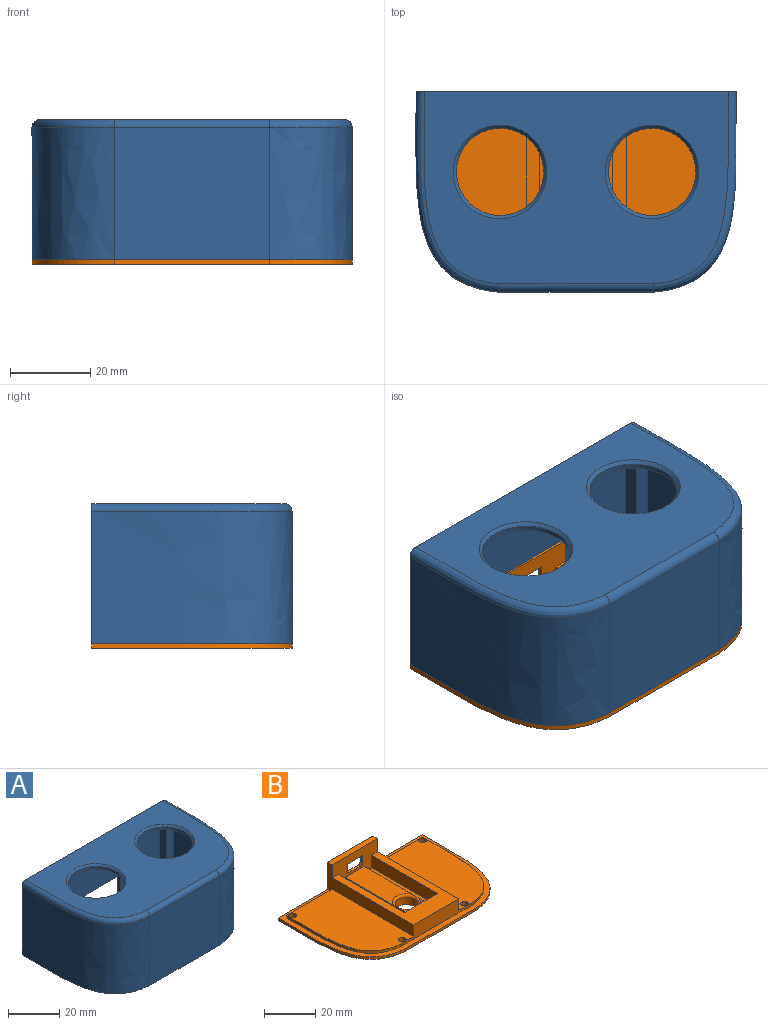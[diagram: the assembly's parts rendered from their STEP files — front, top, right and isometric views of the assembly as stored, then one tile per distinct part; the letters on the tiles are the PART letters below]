
ASSEMBLY  parts=2 mates=1
PART A: 303 faces, bbox 86.4x51x35.1 mm
  f0: plane 80.07x35.07mm, normal (0,1,0), area 2328.1mm2, adj f1,f9,f11,f12,f38,f39,f41,f42
  f1: plane 86.32x50mm, normal (0,0,-1), area 416.2mm2, adj f0,f2,f9,f10,f11,f18,f19,f20
  f2: plane 72.12x33mm, normal (0,-1,0), area 1919mm2, adj f1,f15,f16,f22,f23,f26,f27,f41
  f3: plane 31.4x4mm, normal (1,0,0), area 125.6mm2, adj f4,f15,f18,f29
  f4: plane 31.4x4mm, normal (0,1,0), area 125.6mm2, adj f3,f5,f15,f29
  f5: plane 31.4x4mm, normal (-1,0,0), area 125.6mm2, adj f4,f15,f19,f29
  f6: plane 31.4x4mm, normal (1,0,0), area 125.6mm2, adj f7,f15,f19,f28
  f7: plane 31.4x4mm, normal (0,1,0), area 125.6mm2, adj f6,f8,f15,f28
  f8: plane 31.4x4mm, normal (-1,0,0), area 125.6mm2, adj f7,f15,f20,f28
  f9: extruded ~50x33mm, area 2014.1mm2, adj f0,f1,f10,f38
  f10: plane 38.68x33mm, normal (0,-1,0), area 1276.3mm2, adj f1,f9,f11,f40
  f11: extruded ~50x33mm, area 2014.1mm2, adj f0,f1,f10,f39
  f12: plane 76.13x48.02mm, normal (0,0,1), area 2603mm2, adj f0,f38,f39,f40,f301,f302
  f13: cylinder r=10.9mm len=21.8mm, axis (0,0,1), area 82.2mm2, adj f15,f301
  f14: cylinder r=10.9mm len=21.8mm, axis (0,0,1), area 82.2mm2, adj f15,f302
  f15: plane 76.16x46mm, normal (0,0,-1), area 2501mm2, adj f2,f3,f4,f5,f6,f7,f8,f13
  f16: plane 31.4x4mm, normal (-1,0.03,0), area 125.6mm2, adj f2,f15,f17,f24
  f17: plane 31.4x4mm, normal (0,-1,0), area 125.6mm2, adj f15,f16,f18,f24
  f18: extruded ~42x33mm, area 1715.2mm2, adj f1,f3,f15,f17,f19,f25
  f19: plane 38.51x33mm, normal (0,1,0), area 1019.7mm2, adj f1,f5,f6,f15,f18,f20,f28,f29
  f20: extruded ~42x33mm, area 1715.1mm2, adj f1,f8,f15,f19,f21,f26
  f21: plane 31.4x4mm, normal (0,-1,0), area 125.6mm2, adj f15,f20,f22,f27
  f22: plane 31.4x4mm, normal (1,0,0), area 125.6mm2, adj f2,f15,f21,f27
  f23: plane 3.9x1.6mm, normal (0,-1,0), area 6.2mm2, adj f1,f2,f24,f25
  f24: plane 4x4mm, normal (0,0,-1), area 10.9mm2, adj f16,f17,f23,f25,f36
  f25: plane 4x1.6mm, normal (-1,0,0), area 6.4mm2, adj f1,f18,f23,f24
  f26: plane 4x1.6mm, normal (1,0,0), area 6.4mm2, adj f1,f2,f20,f27
  f27: plane 4x4mm, normal (0,0,-1), area 11.1mm2, adj f2,f21,f22,f26,f34
  f28: plane 4x4mm, normal (0,0,-1), area 11.1mm2, adj f6,f7,f8,f19,f32
  f29: plane 4x4mm, normal (0,0,-1), area 11.1mm2, adj f3,f4,f5,f19,f30
  f30: cylinder r=1.25mm len=23.4mm, axis (0,0,-1), area 183.8mm2, adj f29,f31
  f31: plane 2.5x2.5mm, normal (0,0,-1), area 4.9mm2, adj f30
  f32: cylinder r=1.25mm len=23.4mm, axis (0,0,-1), area 183.8mm2, adj f28,f33
  f33: plane 2.5x2.5mm, normal (0,0,-1), area 4.9mm2, adj f32
  f34: cylinder r=1.25mm len=23.4mm, axis (0,0,-1), area 183.8mm2, adj f27,f35
  f35: plane 2.5x2.5mm, normal (0,0,-1), area 4.9mm2, adj f34
  f36: cylinder r=1.25mm len=23.4mm, axis (0,0,-1), area 183.8mm2, adj f24,f37
  f37: plane 2.5x2.5mm, normal (0,0,-1), area 4.9mm2, adj f36
  f38: bspline ~50.91x21.41mm, area 188.2mm2, adj f0,f9,f12,f40
  f39: bspline ~50.91x21.41mm, area 188.2mm2, adj f0,f11,f12,f40
  f40: cylinder r=2mm len=38.68mm, axis (-1,0,0), area 121.2mm2, adj f10,f12,f38,f39
  f41: plane 13.2x2mm, normal (1,0,0), area 26.4mm2, adj f0,f1,f2,f43
  f42: plane 13.2x2mm, normal (-1,0,0), area 26.4mm2, adj f0,f1,f2,f43
  f43: plane 25.4x2mm, normal (0,0,-1), area 50.8mm2, adj f0,f2,f41,f42
  f44: plane 0.6x0.52mm, normal (-1,0,0), area 0.3mm2, adj f0,f45,f47,f48
  f45: plane 1.69x0.6mm, normal (0,0,1), area 1mm2, adj f0,f44,f46,f48
  f46: plane 0.6x0.52mm, normal (1,0,0), area 0.3mm2, adj f0,f45,f47,f48
  f47: plane 1.69x0.6mm, normal (0,0,-1), area 1mm2, adj f0,f44,f46,f48
  f48: plane 1.69x0.52mm, normal (0,1,0), area 0.9mm2, adj f44,f45,f46,f47
  f49: extruded ~0.84x0.6mm, area 0.6mm2, adj f50,f71,f72,f293
  f50: extruded ~0.8x0.6mm, area 0.5mm2, adj f49,f51,f72,f293
  f51: extruded ~1.1x0.6mm, area 0.7mm2, adj f50,f52,f72,f293
  f52: extruded ~1.1x0.6mm, area 0.7mm2, adj f51,f53,f72,f293
  f53: extruded ~0.79x0.6mm, area 0.5mm2, adj f52,f54,f72,f293
  f54: extruded ~0.85x0.6mm, area 0.6mm2, adj f53,f55,f72,f293
  f55: extruded ~1.14x0.6mm, area 0.7mm2, adj f54,f71,f72,f293
  f56: extruded ~1.16x0.6mm, area 0.8mm2, adj f0,f57,f70,f72
  f57: extruded ~1.19x0.6mm, area 0.8mm2, adj f0,f56,f58,f72
  f58: plane 0.6x0.03mm, normal (0,0,-1), area 0mm2, adj f0,f57,f59,f72
  f59: extruded ~0.79x0.6mm, area 0.5mm2, adj f0,f58,f60,f72
  f60: plane 1.3x0.6mm, normal (1,0,0), area 0.8mm2, adj f0,f59,f61,f72
  f61: plane 0.6x0.57mm, normal (0,0,-1), area 0.3mm2, adj f0,f60,f62,f72
  f62: plane 5.36x0.6mm, normal (-1,0,0), area 3.2mm2, adj f0,f61,f63,f72
  f63: plane 0.6x0.41mm, normal (0,0,1), area 0.2mm2, adj f0,f62,f64,f72
  f64: plane 0.6x0.49mm, normal (0.97,0,0.24), area 0.3mm2, adj f0,f63,f65,f72
  f65: plane 0.6x0.04mm, normal (0,0,1), area 0mm2, adj f0,f64,f66,f72
  f66: extruded ~0.6x0.51mm, area 0.4mm2, adj f0,f65,f67,f72
  f67: extruded ~0.67x0.6mm, area 0.4mm2, adj f0,f66,f68,f72
  f68: extruded ~1.15x0.6mm, area 0.8mm2, adj f0,f67,f69,f72
  f69: extruded ~1.45x0.6mm, area 0.9mm2, adj f0,f68,f70,f72
  f70: extruded ~1.44x0.6mm, area 0.9mm2, adj f0,f56,f69,f72
  f71: extruded ~1.13x0.6mm, area 0.7mm2, adj f49,f55,f72,f293
  f72: plane 5.43x3.33mm, normal (0,1,0), area 6.9mm2, adj f49,f50,f51,f52,f53,f54,f55,f56
  f73: extruded ~1.6x0.6mm, area 1mm2, adj f74,f88,f89,f294
  f74: extruded ~1.6x0.6mm, area 1mm2, adj f73,f75,f89,f294
  f75: extruded ~0.82x0.6mm, area 0.6mm2, adj f74,f76,f89,f294
  f76: extruded ~0.83x0.6mm, area 0.6mm2, adj f75,f77,f89,f294
  f77: extruded ~1.59x0.6mm, area 1mm2, adj f76,f78,f89,f294
  f78: extruded ~1.59x0.6mm, area 1mm2, adj f77,f79,f89,f294
  f79: extruded ~0.83x0.6mm, area 0.6mm2, adj f78,f88,f89,f294
  f80: extruded ~1.95x0.6mm, area 1.2mm2, adj f0,f81,f87,f89
  f81: extruded ~1.93x0.6mm, area 1.2mm2, adj f0,f80,f82,f89
  f82: extruded ~1.25x0.67mm, area 0.9mm2, adj f0,f81,f83,f89
  f83: extruded ~1.25x0.64mm, area 0.9mm2, adj f0,f82,f84,f89
  f84: extruded ~1.95x0.6mm, area 1.2mm2, adj f0,f83,f85,f89
  f85: extruded ~1.94x0.6mm, area 1.2mm2, adj f0,f84,f86,f89
  f86: extruded ~1.24x0.66mm, area 0.9mm2, adj f0,f85,f87,f89
  f87: extruded ~1.26x0.64mm, area 0.9mm2, adj f0,f80,f86,f89
  f88: extruded ~0.82x0.6mm, area 0.6mm2, adj f73,f79,f89,f294
  f89: plane 5.19x3.33mm, normal (0,1,0), area 6.7mm2, adj f73,f74,f75,f76,f77,f78,f79,f80
  f90: extruded ~1.6x0.6mm, area 1mm2, adj f91,f105,f106,f295
  f91: extruded ~1.6x0.6mm, area 1mm2, adj f90,f92,f106,f295
  f92: extruded ~0.82x0.6mm, area 0.6mm2, adj f91,f93,f106,f295
  f93: extruded ~0.83x0.6mm, area 0.6mm2, adj f92,f94,f106,f295
  f94: extruded ~1.59x0.6mm, area 1mm2, adj f93,f95,f106,f295
  f95: extruded ~1.59x0.6mm, area 1mm2, adj f94,f96,f106,f295
  f96: extruded ~0.83x0.6mm, area 0.6mm2, adj f95,f105,f106,f295
  f97: extruded ~1.95x0.6mm, area 1.2mm2, adj f0,f98,f104,f106
  f98: extruded ~1.93x0.6mm, area 1.2mm2, adj f0,f97,f99,f106
  f99: extruded ~1.25x0.67mm, area 0.9mm2, adj f0,f98,f100,f106
  f100: extruded ~1.25x0.64mm, area 0.9mm2, adj f0,f99,f101,f106
  f101: extruded ~1.95x0.6mm, area 1.2mm2, adj f0,f100,f102,f106
  f102: extruded ~1.94x0.6mm, area 1.2mm2, adj f0,f101,f103,f106
  f103: extruded ~1.24x0.66mm, area 0.9mm2, adj f0,f102,f104,f106
  f104: extruded ~1.26x0.64mm, area 0.9mm2, adj f0,f97,f103,f106
  f105: extruded ~0.82x0.6mm, area 0.6mm2, adj f90,f96,f106,f295
  f106: plane 5.19x3.33mm, normal (0,1,0), area 6.7mm2, adj f90,f91,f92,f93,f94,f95,f96,f97
  f107: extruded ~1.6x0.6mm, area 1mm2, adj f108,f122,f123,f296
  f108: extruded ~1.6x0.6mm, area 1mm2, adj f107,f109,f123,f296
  f109: extruded ~0.82x0.6mm, area 0.6mm2, adj f108,f110,f123,f296
  f110: extruded ~0.83x0.6mm, area 0.6mm2, adj f109,f111,f123,f296
  f111: extruded ~1.59x0.6mm, area 1mm2, adj f110,f112,f123,f296
  f112: extruded ~1.59x0.6mm, area 1mm2, adj f111,f113,f123,f296
  f113: extruded ~0.83x0.6mm, area 0.6mm2, adj f112,f122,f123,f296
  f114: extruded ~1.95x0.6mm, area 1.2mm2, adj f0,f115,f121,f123
  f115: extruded ~1.93x0.6mm, area 1.2mm2, adj f0,f114,f116,f123
  f116: extruded ~1.25x0.67mm, area 0.9mm2, adj f0,f115,f117,f123
  f117: extruded ~1.25x0.64mm, area 0.9mm2, adj f0,f116,f118,f123
  f118: extruded ~1.95x0.6mm, area 1.2mm2, adj f0,f117,f119,f123
  f119: extruded ~1.94x0.6mm, area 1.2mm2, adj f0,f118,f120,f123
  f120: extruded ~1.24x0.66mm, area 0.9mm2, adj f0,f119,f121,f123
  f121: extruded ~1.26x0.64mm, area 0.9mm2, adj f0,f114,f120,f123
  f122: extruded ~0.82x0.6mm, area 0.6mm2, adj f107,f113,f123,f296
  f123: plane 5.19x3.33mm, normal (0,1,0), area 6.7mm2, adj f107,f108,f109,f110,f111,f112,f113,f114
  f124: extruded ~1.6x0.6mm, area 1mm2, adj f125,f139,f140,f297
  f125: extruded ~1.6x0.6mm, area 1mm2, adj f124,f126,f140,f297
  f126: extruded ~0.82x0.6mm, area 0.6mm2, adj f125,f127,f140,f297
  f127: extruded ~0.83x0.6mm, area 0.6mm2, adj f126,f128,f140,f297
  f128: extruded ~1.59x0.6mm, area 1mm2, adj f127,f129,f140,f297
  f129: extruded ~1.59x0.6mm, area 1mm2, adj f128,f130,f140,f297
  f130: extruded ~0.83x0.6mm, area 0.6mm2, adj f129,f139,f140,f297
  f131: extruded ~1.95x0.6mm, area 1.2mm2, adj f0,f132,f138,f140
  f132: extruded ~1.93x0.6mm, area 1.2mm2, adj f0,f131,f133,f140
  f133: extruded ~1.25x0.67mm, area 0.9mm2, adj f0,f132,f134,f140
  f134: extruded ~1.25x0.64mm, area 0.9mm2, adj f0,f133,f135,f140
  f135: extruded ~1.95x0.6mm, area 1.2mm2, adj f0,f134,f136,f140
  f136: extruded ~1.94x0.6mm, area 1.2mm2, adj f0,f135,f137,f140
  f137: extruded ~1.24x0.66mm, area 0.9mm2, adj f0,f136,f138,f140
  f138: extruded ~1.26x0.64mm, area 0.9mm2, adj f0,f131,f137,f140
  f139: extruded ~0.82x0.6mm, area 0.6mm2, adj f124,f130,f140,f297
  f140: plane 5.19x3.33mm, normal (0,1,0), area 6.7mm2, adj f124,f125,f126,f127,f128,f129,f130,f131
  f141: extruded ~1.6x0.6mm, area 1mm2, adj f142,f156,f157,f298
  f142: extruded ~1.6x0.6mm, area 1mm2, adj f141,f143,f157,f298
  f143: extruded ~0.82x0.6mm, area 0.6mm2, adj f142,f144,f157,f298
  f144: extruded ~0.83x0.6mm, area 0.6mm2, adj f143,f145,f157,f298
  f145: extruded ~1.59x0.6mm, area 1mm2, adj f144,f146,f157,f298
  f146: extruded ~1.59x0.6mm, area 1mm2, adj f145,f147,f157,f298
  f147: extruded ~0.83x0.6mm, area 0.6mm2, adj f146,f156,f157,f298
  f148: extruded ~1.95x0.6mm, area 1.2mm2, adj f0,f149,f155,f157
  f149: extruded ~1.93x0.6mm, area 1.2mm2, adj f0,f148,f150,f157
  f150: extruded ~1.25x0.67mm, area 0.9mm2, adj f0,f149,f151,f157
  f151: extruded ~1.25x0.64mm, area 0.9mm2, adj f0,f150,f152,f157
  f152: extruded ~1.95x0.6mm, area 1.2mm2, adj f0,f151,f153,f157
  f153: extruded ~1.94x0.6mm, area 1.2mm2, adj f0,f152,f154,f157
  f154: extruded ~1.24x0.66mm, area 0.9mm2, adj f0,f153,f155,f157
  f155: extruded ~1.26x0.64mm, area 0.9mm2, adj f0,f148,f154,f157
  f156: extruded ~0.82x0.6mm, area 0.6mm2, adj f141,f147,f157,f298
  f157: plane 5.19x3.33mm, normal (0,1,0), area 6.7mm2, adj f141,f142,f143,f144,f145,f146,f147,f148
  f158: extruded ~1.6x0.6mm, area 1mm2, adj f159,f173,f174,f299
  f159: extruded ~1.6x0.6mm, area 1mm2, adj f158,f160,f174,f299
  f160: extruded ~0.82x0.6mm, area 0.6mm2, adj f159,f161,f174,f299
  f161: extruded ~0.83x0.6mm, area 0.6mm2, adj f160,f162,f174,f299
  f162: extruded ~1.59x0.6mm, area 1mm2, adj f161,f163,f174,f299
  f163: extruded ~1.59x0.6mm, area 1mm2, adj f162,f164,f174,f299
  f164: extruded ~0.83x0.6mm, area 0.6mm2, adj f163,f173,f174,f299
  f165: extruded ~1.95x0.6mm, area 1.2mm2, adj f0,f166,f172,f174
  f166: extruded ~1.93x0.6mm, area 1.2mm2, adj f0,f165,f167,f174
  f167: extruded ~1.25x0.67mm, area 0.9mm2, adj f0,f166,f168,f174
  f168: extruded ~1.25x0.64mm, area 0.9mm2, adj f0,f167,f169,f174
  f169: extruded ~1.95x0.6mm, area 1.2mm2, adj f0,f168,f170,f174
  f170: extruded ~1.94x0.6mm, area 1.2mm2, adj f0,f169,f171,f174
  f171: extruded ~1.24x0.66mm, area 0.9mm2, adj f0,f170,f172,f174
  f172: extruded ~1.26x0.64mm, area 0.9mm2, adj f0,f165,f171,f174
  f173: extruded ~0.82x0.6mm, area 0.6mm2, adj f158,f164,f174,f299
  f174: plane 5.19x3.33mm, normal (0,1,0), area 6.7mm2, adj f158,f159,f160,f161,f162,f163,f164,f165
  f175: plane 0.6x0.56mm, normal (0,0,1), area 0.3mm2, adj f0,f176,f183,f184
  f176: plane 5.04x0.6mm, normal (1,0,0), area 3mm2, adj f0,f175,f177,f184
  f177: plane 0.6x0.48mm, normal (0,0,-1), area 0.3mm2, adj f0,f176,f178,f184
  f178: plane 1.33x1.03mm, normal (-0.61,0,-0.79), area 1mm2, adj f0,f177,f179,f184
  f179: plane 0.6x0.39mm, normal (-0.79,0,0.61), area 0.3mm2, adj f0,f178,f180,f184
  f180: extruded ~0.82x0.67mm, area 0.6mm2, adj f0,f179,f181,f184
  f181: extruded ~0.6x0.16mm, area 0.1mm2, adj f0,f180,f182,f184
  f182: extruded ~0.85x0.6mm, area 0.5mm2, adj f0,f181,f183,f184
  f183: plane 3.59x0.6mm, normal (-1,0,0), area 2.2mm2, adj f0,f175,f182,f184
  f184: plane 5.04x1.81mm, normal (0,1,0), area 3.5mm2, adj f175,f176,f177,f178,f179,f180,f181,f182
  f185: plane 3.31x0.6mm, normal (0,0,1), area 2mm2, adj f0,f186,f204,f205
  f186: plane 0.6x0.53mm, normal (1,0,0), area 0.3mm2, adj f0,f185,f187,f205
  f187: plane 2.59x0.6mm, normal (0,0,-1), area 1.6mm2, adj f0,f186,f188,f205
  f188: plane 0.6x0.03mm, normal (1,0,0), area 0mm2, adj f0,f187,f189,f205
  f189: plane 1.1x1.08mm, normal (0.7,0,0.71), area 0.9mm2, adj f0,f188,f190,f205
  f190: extruded ~1.19x1.01mm, area 0.9mm2, adj f0,f189,f191,f205
  f191: extruded ~0.95x0.6mm, area 0.6mm2, adj f0,f190,f192,f205
  f192: extruded ~0.98x0.6mm, area 0.7mm2, adj f0,f191,f193,f205
  f193: extruded ~1.11x0.6mm, area 0.7mm2, adj f0,f192,f194,f205
  f194: extruded ~1.52x0.6mm, area 1mm2, adj f0,f193,f195,f205
  f195: plane 0.6x0.39mm, normal (-0.79,0,0.61), area 0.3mm2, adj f0,f194,f196,f205
  f196: extruded ~0.63x0.6mm, area 0.4mm2, adj f0,f195,f197,f205
  f197: extruded ~0.6x0.59mm, area 0.4mm2, adj f0,f196,f198,f205
  f198: extruded ~0.68x0.6mm, area 0.4mm2, adj f0,f197,f199,f205
  f199: extruded ~0.64x0.6mm, area 0.4mm2, adj f0,f198,f200,f205
  f200: extruded ~0.6x0.53mm, area 0.3mm2, adj f0,f199,f201,f205
  f201: extruded ~0.6x0.51mm, area 0.4mm2, adj f0,f200,f202,f205
  f202: extruded ~0.88x0.8mm, area 0.7mm2, adj f0,f201,f203,f205
  f203: plane 1.33x1.33mm, normal (-0.71,0,-0.71), area 1.1mm2, adj f0,f202,f204,f205
  f204: plane 0.6x0.49mm, normal (-1,0,0), area 0.3mm2, adj f0,f185,f203,f205
  f205: plane 5.11x3.31mm, normal (0,1,0), area 5.6mm2, adj f185,f186,f187,f188,f189,f190,f191,f192
  f206: extruded ~0.79x0.6mm, area 0.5mm2, adj f0,f207,f233,f234
  f207: extruded ~0.92x0.6mm, area 0.6mm2, adj f0,f206,f208,f234
  f208: extruded ~1.14x0.6mm, area 0.7mm2, adj f0,f207,f209,f234
  f209: extruded ~0.85x0.6mm, area 0.5mm2, adj f0,f208,f210,f234
  f210: extruded ~0.71x0.6mm, area 0.5mm2, adj f0,f209,f211,f234
  f211: plane 0.6x0.39mm, normal (-0.8,0,0.6), area 0.3mm2, adj f0,f210,f212,f234
  f212: extruded ~0.67x0.6mm, area 0.4mm2, adj f0,f211,f213,f234
  f213: extruded ~0.62x0.6mm, area 0.4mm2, adj f0,f212,f214,f234
  f214: extruded ~0.69x0.6mm, area 0.4mm2, adj f0,f213,f215,f234
  f215: extruded ~0.6x0.58mm, area 0.4mm2, adj f0,f214,f216,f234
  f216: extruded ~0.72x0.6mm, area 0.5mm2, adj f0,f215,f217,f234
  f217: extruded ~0.93x0.6mm, area 0.6mm2, adj f0,f216,f218,f234
  f218: plane 0.6x0.5mm, normal (0,0,-1), area 0.3mm2, adj f0,f217,f219,f234
  f219: plane 0.6x0.49mm, normal (-1,0,0), area 0.3mm2, adj f0,f218,f220,f234
  f220: plane 0.6x0.5mm, normal (0,0,1), area 0.3mm2, adj f0,f219,f221,f234
  f221: extruded ~1.44x0.92mm, area 1.2mm2, adj f0,f220,f222,f234
  f222: extruded ~1.31x1.02mm, area 1.1mm2, adj f0,f221,f223,f234
  f223: extruded ~0.7x0.6mm, area 0.4mm2, adj f0,f222,f224,f234
  f224: extruded ~0.7x0.6mm, area 0.4mm2, adj f0,f223,f225,f234
  f225: plane 0.6x0.54mm, normal (-1,0,0), area 0.3mm2, adj f0,f224,f226,f234
  f226: extruded ~0.65x0.6mm, area 0.4mm2, adj f0,f225,f227,f234
  f227: extruded ~0.73x0.6mm, area 0.4mm2, adj f0,f226,f228,f234
  f228: extruded ~1.42x0.6mm, area 0.9mm2, adj f0,f227,f229,f234
  f229: extruded ~1.11x0.6mm, area 0.8mm2, adj f0,f228,f230,f234
  f230: extruded ~0.81x0.6mm, area 0.5mm2, adj f0,f229,f231,f234
  f231: extruded ~0.9x0.6mm, area 0.6mm2, adj f0,f230,f232,f234
  f232: plane 0.6x0.03mm, normal (1,0,0), area 0mm2, adj f0,f231,f233,f234
  f233: extruded ~0.77x0.6mm, area 0.5mm2, adj f0,f206,f232,f234
  f234: plane 5.18x3.3mm, normal (0,1,0), area 5.9mm2, adj f206,f207,f208,f209,f210,f211,f212,f213
  f235: plane 0.6x0.52mm, normal (-1,0,0), area 0.3mm2, adj f0,f236,f238,f239
  f236: plane 1.69x0.6mm, normal (0,0,1), area 1mm2, adj f0,f235,f237,f239
  f237: plane 0.6x0.52mm, normal (1,0,0), area 0.3mm2, adj f0,f236,f238,f239
  f238: plane 1.69x0.6mm, normal (0,0,-1), area 1mm2, adj f0,f235,f237,f239
  f239: plane 1.69x0.52mm, normal (0,1,0), area 0.9mm2, adj f235,f236,f237,f238
  f240: extruded ~0.76x0.6mm, area 0.5mm2, adj f241,f265,f266,f300
  f241: extruded ~0.6x0.58mm, area 0.4mm2, adj f240,f242,f266,f300
  f242: extruded ~0.6x0.48mm, area 0.4mm2, adj f241,f243,f266,f300
  f243: extruded ~0.67x0.6mm, area 0.4mm2, adj f242,f244,f266,f300
  f244: extruded ~0.6x0.46mm, area 0.3mm2, adj f243,f245,f266,f300
  f245: extruded ~0.6x0.42mm, area 0.3mm2, adj f244,f246,f266,f300
  f246: extruded ~0.6x0.58mm, area 0.4mm2, adj f245,f247,f266,f300
  f247: extruded ~0.75x0.6mm, area 0.5mm2, adj f246,f248,f266,f300
  f248: extruded ~0.78x0.6mm, area 0.5mm2, adj f247,f265,f266,f300
  f249: extruded ~2.96x2.29mm, area 2.6mm2, adj f0,f250,f264,f266
  f250: extruded ~1.19x0.6mm, area 0.7mm2, adj f0,f249,f251,f266
  f251: extruded ~0.77x0.6mm, area 0.6mm2, adj f0,f250,f252,f266
  f252: extruded ~0.9x0.6mm, area 0.6mm2, adj f0,f251,f253,f266
  f253: extruded ~1.16x0.6mm, area 0.8mm2, adj f0,f252,f254,f266
  f254: extruded ~1.24x0.6mm, area 0.8mm2, adj f0,f253,f255,f266
  f255: extruded ~1.12x0.6mm, area 0.7mm2, adj f0,f254,f256,f266
  f256: extruded ~1.06x0.6mm, area 0.7mm2, adj f0,f255,f257,f266
  f257: extruded ~0.71x0.6mm, area 0.4mm2, adj f0,f256,f258,f266
  f258: extruded ~0.6x0.5mm, area 0.4mm2, adj f0,f257,f259,f266
  f259: plane 0.6x0.04mm, normal (0,0,1), area 0mm2, adj f0,f258,f260,f266
  f260: extruded ~1.57x0.6mm, area 1mm2, adj f0,f259,f261,f266
  f261: extruded ~1.25x0.6mm, area 0.8mm2, adj f0,f260,f262,f266
  f262: extruded ~0.63x0.6mm, area 0.4mm2, adj f0,f261,f263,f266
  f263: plane 0.6x0.49mm, normal (-1,0,0), area 0.3mm2, adj f0,f262,f264,f266
  f264: extruded ~0.63x0.6mm, area 0.4mm2, adj f0,f249,f263,f266
  f265: extruded ~0.88x0.6mm, area 0.6mm2, adj f240,f248,f266,f300
  f266: plane 5.18x3.29mm, normal (0,1,0), area 6.6mm2, adj f240,f241,f242,f243,f244,f245,f246,f247
  f267: plane 0.6x0.56mm, normal (0,0,1), area 0.3mm2, adj f0,f268,f275,f276
  f268: plane 5.04x0.6mm, normal (1,0,0), area 3mm2, adj f0,f267,f269,f276
  f269: plane 0.6x0.48mm, normal (0,0,-1), area 0.3mm2, adj f0,f268,f270,f276
  f270: plane 1.33x1.03mm, normal (-0.61,0,-0.79), area 1mm2, adj f0,f269,f271,f276
  f271: plane 0.6x0.39mm, normal (-0.79,0,0.61), area 0.3mm2, adj f0,f270,f272,f276
  f272: extruded ~0.82x0.67mm, area 0.6mm2, adj f0,f271,f273,f276
  f273: extruded ~0.6x0.16mm, area 0.1mm2, adj f0,f272,f274,f276
  f274: extruded ~0.85x0.6mm, area 0.5mm2, adj f0,f273,f275,f276
  f275: plane 3.59x0.6mm, normal (-1,0,0), area 2.2mm2, adj f0,f267,f274,f276
  f276: plane 5.04x1.81mm, normal (0,1,0), area 3.5mm2, adj f267,f268,f269,f270,f271,f272,f273,f274
  f277: plane 3.78x1.43mm, normal (-0.93,0,0.35), area 2.4mm2, adj f0,f278,f286,f287
  f278: plane 0.67x0.6mm, normal (0,0,1), area 0.4mm2, adj f0,f277,f279,f287
  f279: plane 3.78x1.43mm, normal (0.93,0,0.35), area 2.4mm2, adj f0,f278,f280,f287
  f280: plane 0.61x0.6mm, normal (0,0,-1), area 0.4mm2, adj f0,f279,f281,f287
  f281: extruded ~2.5x0.9mm, area 1.6mm2, adj f0,f280,f282,f287
  f282: extruded ~0.76x0.6mm, area 0.5mm2, adj f0,f281,f283,f287
  f283: plane 0.6x0.03mm, normal (0,0,-1), area 0mm2, adj f0,f282,f284,f287
  f284: extruded ~1.02x0.6mm, area 0.6mm2, adj f0,f283,f285,f287
  f285: plane 2.24x0.81mm, normal (0.94,0,-0.34), area 1.4mm2, adj f0,f284,f286,f287
  f286: plane 0.61x0.6mm, normal (0,0,-1), area 0.4mm2, adj f0,f277,f285,f287
  f287: plane 3.78x3.53mm, normal (0,1,0), area 4.2mm2, adj f277,f278,f279,f280,f281,f282,f283,f284
  f288: plane 3.19x0.6mm, normal (0,0,1), area 1.9mm2, adj f0,f289,f291,f292
  f289: plane 0.6x0.45mm, normal (1,0,0), area 0.3mm2, adj f0,f288,f290,f292
  f290: plane 3.19x0.6mm, normal (0,0,-1), area 1.9mm2, adj f0,f289,f291,f292
  f291: plane 0.6x0.45mm, normal (-1,0,0), area 0.3mm2, adj f0,f288,f290,f292
  f292: plane 3.19x0.45mm, normal (0,1,0), area 1.4mm2, adj f288,f289,f290,f291
  f293: plane 2.95x2.16mm, normal (0,1,0), area 5.4mm2, adj f49,f50,f51,f52,f53,f54,f55,f71
  f294: plane 4.2x2.17mm, normal (0,1,0), area 7.7mm2, adj f73,f74,f75,f76,f77,f78,f79,f88
  f295: plane 4.2x2.17mm, normal (0,1,0), area 7.7mm2, adj f90,f91,f92,f93,f94,f95,f96,f105
  f296: plane 4.2x2.17mm, normal (0,1,0), area 7.7mm2, adj f107,f108,f109,f110,f111,f112,f113,f122
  f297: plane 4.2x2.17mm, normal (0,1,0), area 7.7mm2, adj f124,f125,f126,f127,f128,f129,f130,f139
  f298: plane 4.2x2.17mm, normal (0,1,0), area 7.7mm2, adj f141,f142,f143,f144,f145,f146,f147,f156
  f299: plane 4.2x2.17mm, normal (0,1,0), area 7.7mm2, adj f158,f159,f160,f161,f162,f163,f164,f173
  f300: plane 2.26x2.15mm, normal (0,1,0), area 3.9mm2, adj f240,f241,f242,f243,f244,f245,f246,f247
  f301: cone r=10.9mm half-angle=45deg, axis (0,0,1), area 80.3mm2, adj f12,f13
  f302: cone r=10.9mm half-angle=45deg, axis (0,0,1), area 80.3mm2, adj f12,f14
PART B: 53 faces, bbox 86.3x50x14.2 mm
  f0: plane 26.91x10.4mm, normal (0,0,1), area 251.7mm2, adj f21,f23,f33,f52
  f1: plane 86.32x50mm, normal (0,0,1), area 497.2mm2, adj f2,f6,f7,f8,f9,f11,f12,f13
  f2: plane 25.09x1.2mm, normal (0,1,0), area 30.1mm2, adj f1,f14,f15,f16
  f3: plane 18.4x5.9mm, normal (0,1,0), area 70.1mm2, adj f4,f18,f19,f20,f21,f22,f23,f24
  f4: plane 10.4x6.21mm, normal (0,0,1), area 36.4mm2, adj f3,f21,f23,f52
  f5: plane 45.2x25.18mm, normal (0,0,1), area 1031.5mm2, adj f11,f12,f13,f17,f31,f32
  f6: plane 80x14.2mm, normal (0,1,0), area 209.4mm2, adj f1,f7,f9,f10,f16,f17,f34,f43
  f7: extruded ~50x20.73mm, area 73.2mm2, adj f1,f6,f8,f10
  f8: plane 38.68x1.2mm, normal (0,-1,0), area 46.4mm2, adj f1,f7,f9,f10
  f9: extruded ~50x20.73mm, area 73.2mm2, adj f1,f6,f8,f10
  f10: plane 86.32x50mm, normal (0,0,-1), area 3686.5mm2, adj f6,f7,f8,f9,f29,f30,f31,f32
  f11: plane 25.09x1.2mm, normal (0,1,0), area 30.1mm2, adj f1,f5,f12,f17
  f12: extruded ~45.2x18.42mm, area 66mm2, adj f1,f5,f11,f13
  f13: plane 38.48x6.7mm, normal (0,-1,0), area 183.7mm2, adj f1,f5,f12,f14,f15,f16,f17,f18
  f14: extruded ~45.2x18.42mm, area 66mm2, adj f1,f2,f13,f15
  f15: plane 45.2x25.18mm, normal (0,0,1), area 1031.5mm2, adj f2,f13,f14,f16,f29,f30
  f16: plane 47.6x13mm, normal (1,0,0), area 279.8mm2, adj f1,f2,f6,f13,f15,f18,f33,f34
  f17: plane 47.6x13mm, normal (-1,0,0), area 279.8mm2, adj f1,f5,f6,f11,f13,f18,f33,f34
  f18: plane 45.2x25mm, normal (0,0,1), area 454.7mm2, adj f3,f13,f16,f17,f19,f20,f26,f33
  f19: plane 36.7x5.9mm, normal (1,0,0), area 216.5mm2, adj f3,f18,f22,f33
  f20: plane 36.7x5.9mm, normal (-1,0,0), area 216.5mm2, adj f3,f18,f24,f33
  f21: plane 36.7x2.5mm, normal (-1,0,0), area 91.7mm2, adj f0,f3,f4,f22,f33,f52
  f22: plane 36.7x4mm, normal (0,0,1), area 146.8mm2, adj f3,f19,f21,f33
  f23: plane 36.7x2.5mm, normal (1,0,0), area 91.7mm2, adj f0,f3,f4,f24,f33,f52
  f24: plane 36.7x4mm, normal (0,0,1), area 146.8mm2, adj f3,f20,f23,f33
  f25: plane 1.2x1.2mm, normal (-1,0,0), area 0.7mm2, adj f3,f26,f27
  f26: plane 10.4x1.2mm, normal (0,0.71,0.71), area 17.6mm2, adj f18,f25,f27,f28
  f27: plane 10.4x1.2mm, normal (0,0,-1), area 12.5mm2, adj f3,f25,f26,f28
  f28: plane 1.2x1.2mm, normal (1,0,0), area 0.7mm2, adj f3,f26,f27
  f29: cylinder r=1.5mm len=3mm, axis (0,0,-1), area 22.6mm2, adj f10,f15
  f30: cylinder r=1.5mm len=3mm, axis (0,0,-1), area 22.6mm2, adj f10,f15
  f31: cylinder r=1.5mm len=3mm, axis (0,0,-1), area 22.6mm2, adj f5,f10
  f32: cylinder r=1.5mm len=3mm, axis (0,0,-1), area 22.6mm2, adj f5,f10
  f33: plane 25x12.2mm, normal (0,-1,0), area 201.8mm2, adj f0,f16,f17,f18,f19,f20,f21,f22
  f34: plane 25x2.4mm, normal (0,0,1), area 60mm2, adj f6,f16,f17,f33
  f35: plane 15x10mm, normal (0,1,0), area 119.3mm2, adj f36,f37,f38,f39,f40,f41,f43,f44
  f36: cylinder r=1mm len=1.2mm, axis (0,1,0), area 1.9mm2, adj f33,f35,f37,f41
  f37: plane 3.6x1.2mm, normal (1,0,0), area 3.6mm2, adj f33,f35,f36,f38,f42
  f38: plane 8.4x0.2mm, normal (0,0,-1), area 1.7mm2, adj f35,f37,f39,f42
  f39: plane 3.6x1.2mm, normal (-1,0,0), area 3.6mm2, adj f33,f35,f38,f40,f42
  f40: cylinder r=1mm len=1.2mm, axis (0,1,0), area 1.9mm2, adj f33,f35,f39,f41
  f41: plane 6.4x1.2mm, normal (0,0,1), area 7.7mm2, adj f33,f35,f36,f40
  f42: plane 8.4x1mm, normal (0,-0.71,-0.71), area 11.9mm2, adj f33,f37,f38,f39
  f43: plane 13x1.2mm, normal (0,0.71,-0.71), area 22.1mm2, adj f6,f35,f44,f45
  f44: cone r=1mm half-angle=45deg, axis (0,1,0), area 4.3mm2, adj f6,f35,f43,f46
  f45: cone r=1mm half-angle=45deg, axis (0,1,0), area 4.3mm2, adj f6,f35,f43,f47
  f46: plane 8x1.2mm, normal (0.71,0.71,0), area 13.6mm2, adj f6,f35,f44,f48
  f47: plane 8x1.2mm, normal (-0.71,0.71,0), area 13.6mm2, adj f6,f35,f45,f49
  f48: cone r=1mm half-angle=45deg, axis (0,1,0), area 4.3mm2, adj f6,f35,f46,f50
  f49: cone r=1mm half-angle=45deg, axis (0,1,0), area 4.3mm2, adj f6,f35,f47,f50
  f50: plane 13x1.2mm, normal (0,0.71,0.71), area 22.1mm2, adj f6,f35,f48,f49
  f51: cylinder r=4.5mm len=9mm, axis (0,0,-1), area 99mm2, adj f10,f52
  f52: torus R=5.5mm, axis (0,0,1), area 46.5mm2, adj f0,f4,f21,f23,f51
PLACE A t=(19.92,-2.93,-34.41)mm
PLACE B t=(19.92,-2.93,-35.61)mm
MATE fastened B.f1 <-> A.f1  axis (0,0,1) through (-18.61,13.76,-34.41)mm
